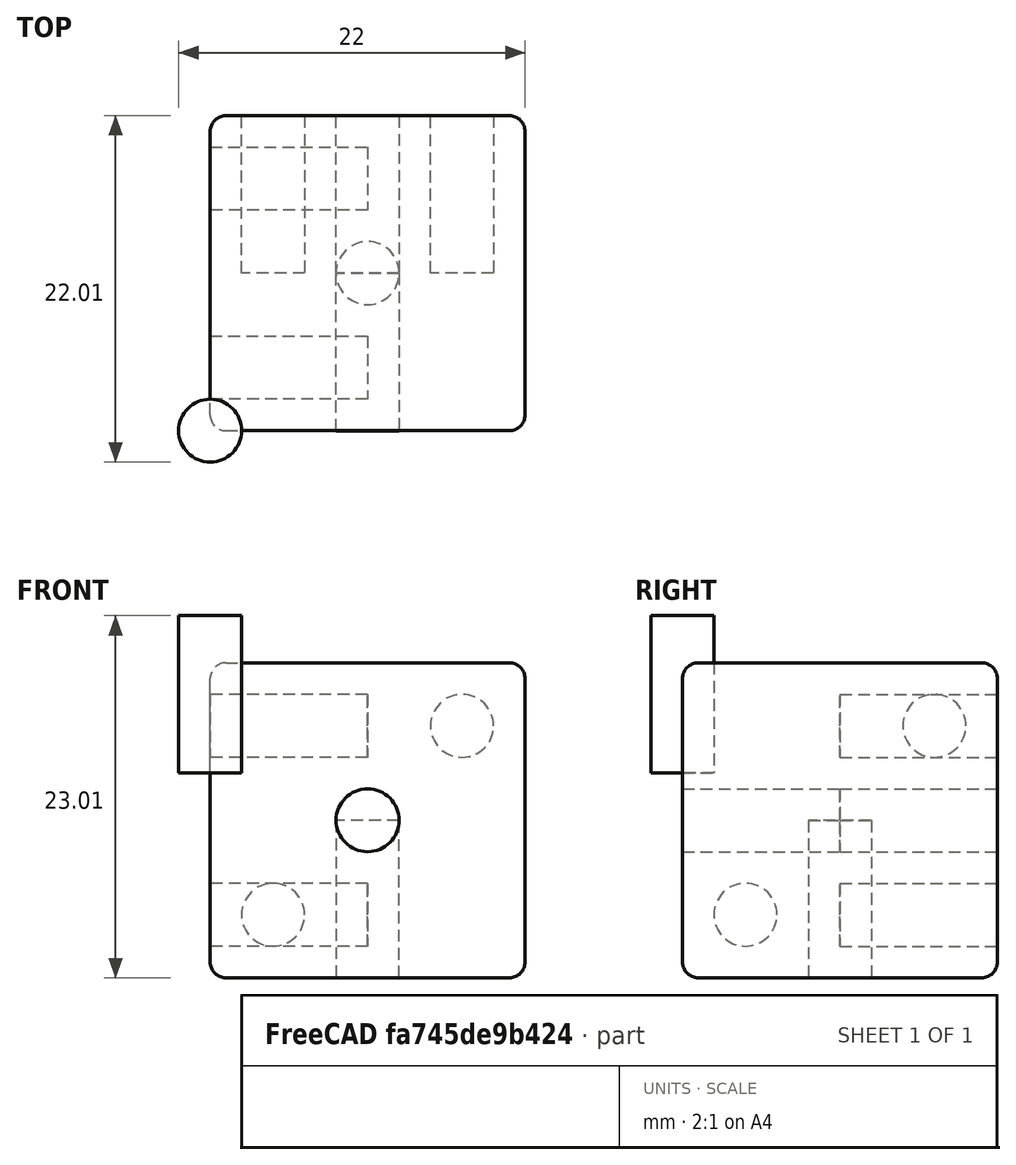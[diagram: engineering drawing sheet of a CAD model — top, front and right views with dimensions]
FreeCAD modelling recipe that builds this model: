
FCSTD DOCUMENT  (FreeCAD 0.21R33694 (Git))
Label: OJT1_T13P03.dau
License: All rights reserved
LicenseURL: http://en.wikipedia.org/wiki/All_rights_reserved
objects: Part::Cylinder×10, Part::FeaturePython×3, Part::Fuse×2, Part::Box×1, Part::Fillet×1
note: 14 computed .brp shape members not serialized (recipe doc carries the construction recipe); baked Part::Feature solids carry a one-line shape summary decoded from their .brp

FEATURE [Part::Box] Box  label="Cub"
  AttacherType = Attacher::AttachEngine3D
  Height = 20
  Length = 20
  Width = 20
FEATURE [Part::Fillet] Fillet
  Base = -> Box
  Edges = 12 edges r=1: [Edge1,Edge2,Edge3,Edge4,Edge5,Edge6,Edge7,Edge8,Edge9,Edge10,Edge11,Edge12]
FEATURE [Part::Cylinder] Cylinder  label="Cilindre"
  Angle = 360
  AttacherType = Attacher::AttachEngine3D
  FirstAngle = 0
  Height = 10
  Placement = pos=(0,0,13) rot=(0,0,1;0rad)
  Radius = 2
  SecondAngle = 0
FEATURE [Part::FeaturePython] Array  # Draft array (typed FeaturePython)
  AlwaysSyncPlacement = false
  Angle = 360
  ArrayType = 0
  Axis = (0,0,1)
  Base = -> Cylinder
  Center = (0,0,0)
  Count = 6
  ExpandArray = false
  Fuse = false
  IntervalAxis = (0,0,0)
  IntervalX = (6,0,0)
  IntervalY = (0,12,0)
  IntervalZ = (0,0,100)
  NumberCircles = 3
  NumberPolar = 5
  NumberX = 3
  NumberY = 2
  NumberZ = 1
  Placement = pos=(4,4,-2.99) rot=(0,0,1;0rad)
  PlacementList = 6 placements: [(0,0,13),(0,12,13),(6,0,13),(6,12,13),(12,0,13),(12,12,13)]
  RadialDistance = 50
  ScaleList = (6) [(1,1,1),(1,1,1),(1,1,1),(1,1,1),(1,1,1),(1,1,1)]
  Symmetry = 1
  TangentialDistance = 25
FEATURE [Part::Cylinder] Cylinder001  label="Cilindre001"
  Angle = 360
  AttacherType = Attacher::AttachEngine3D
  FirstAngle = 0
  Height = 10
  Placement = pos=(0,0,13) rot=(0,0,1;0rad)
  Radius = 2
  SecondAngle = 0
FEATURE [Part::FeaturePython] Array001  # Draft array (typed FeaturePython)
  AlwaysSyncPlacement = false
  Angle = 360
  ArrayType = 0
  Axis = (0,0,1)
  Base = -> Cylinder001
  Center = (0,0,0)
  Count = 4
  ExpandArray = false
  Fuse = false
  IntervalAxis = (0,0,0)
  IntervalX = (12,0,0)
  IntervalY = (0,12,0)
  IntervalZ = (0,0,100)
  NumberCircles = 3
  NumberPolar = 5
  NumberX = 2
  NumberY = 2
  NumberZ = 1
  Placement = pos=(-2.99,4,16) rot=(0,1,0;1.5708rad)
  PlacementList = 4 placements: [(0,0,13),(0,12,13),(12,0,13),(12,12,13)]
  RadialDistance = 50
  ScaleList = (4) [(1,1,1),(1,1,1),(1,1,1),(1,1,1)]
  Symmetry = 1
  TangentialDistance = 25
FEATURE [Part::Cylinder] Cylinder002  label="Cilindre002"
  Angle = 360
  AttacherType = Attacher::AttachEngine3D
  FirstAngle = 0
  Height = 10
  Placement = pos=(0,0,13) rot=(0,0,1;0rad)
  Radius = 2
  SecondAngle = 0
FEATURE [Part::FeaturePython] Array002  # Draft array (typed FeaturePython)
  AlwaysSyncPlacement = false
  Angle = 360
  ArrayType = 0
  Axis = (0,0,1)
  Base = -> Cylinder002
  Center = (0,0,0)
  Count = 4
  ExpandArray = false
  Fuse = false
  IntervalAxis = (0,0,0)
  IntervalX = (12,0,0)
  IntervalY = (0,12,0)
  IntervalZ = (0,0,100)
  NumberCircles = 3
  NumberPolar = 5
  NumberX = 2
  NumberY = 2
  NumberZ = 1
  Placement = pos=(4,22.99,16) rot=(-0.57735,-0.57735,0.57735;4.18879rad)
  PlacementList = 4 placements: [(0,0,13),(0,12,13),(12,0,13),(12,12,13)]
  RadialDistance = 50
  ScaleList = (4) [(1,1,1),(1,1,1),(1,1,1),(1,1,1)]
  Symmetry = 1
  TangentialDistance = 25
FEATURE [Part::Cylinder] Cylinder003  label="Cilindre003"
  Angle = 360
  AttacherType = Attacher::AttachEngine3D
  FirstAngle = 0
  Height = 10
  Placement = pos=(10,9.99,10) rot=(1,0,0;1.5708rad)
  Radius = 2
  SecondAngle = 0
FEATURE [Part::Cylinder] Cylinder004  label="Cilindre004"
  Angle = 360
  AttacherType = Attacher::AttachEngine3D
  FirstAngle = 0
  Height = 10
  Placement = pos=(10,20.01,10) rot=(1,0,0;1.5708rad)
  Radius = 2
  SecondAngle = 0
FEATURE [Part::Cylinder] Cylinder005  label="Cilindre005"
  Angle = 360
  AttacherType = Attacher::AttachEngine3D
  FirstAngle = 0
  Height = 10
  Placement = pos=(16,20.01,16) rot=(1,0,0;1.5708rad)
  Radius = 2
  SecondAngle = 0
FEATURE [Part::Cylinder] Cylinder006  label="Cilindre006"
  Angle = 360
  AttacherType = Attacher::AttachEngine3D
  FirstAngle = 0
  Height = 10
  Placement = pos=(4,20.01,4) rot=(1,0,0;1.5708rad)
  Radius = 2
  SecondAngle = 0
FEATURE [Part::Fuse] Fusion
  Base = -> Cylinder005
  Refine = true
  Tool = -> Cylinder006
FEATURE [Part::Cylinder] Cylinder007  label="Cilindre007"
  Angle = 360
  AttacherType = Attacher::AttachEngine3D
  FirstAngle = 0
  Height = 10
  Placement = pos=(16,20.01,16) rot=(1,0,0;1.5708rad)
  Radius = 2
  SecondAngle = 0
FEATURE [Part::Cylinder] Cylinder008  label="Cilindre008"
  Angle = 360
  AttacherType = Attacher::AttachEngine3D
  FirstAngle = 0
  Height = 10
  Placement = pos=(4,20.01,4) rot=(1,0,0;1.5708rad)
  Radius = 2
  SecondAngle = 0
FEATURE [Part::Fuse] Fusion001
  Base = -> Cylinder007
  Placement = pos=(20,0,0) rot=(0,0,1;1.5708rad)
  Refine = true
  Tool = -> Cylinder008
FEATURE [Part::Cylinder] Cylinder009  label="Cilindre009"
  Angle = 360
  AttacherType = Attacher::AttachEngine3D
  FirstAngle = 0
  Height = 10
  Placement = pos=(10,10.01,-0.01) rot=(0,0,1;0rad)
  Radius = 2
  SecondAngle = 0
